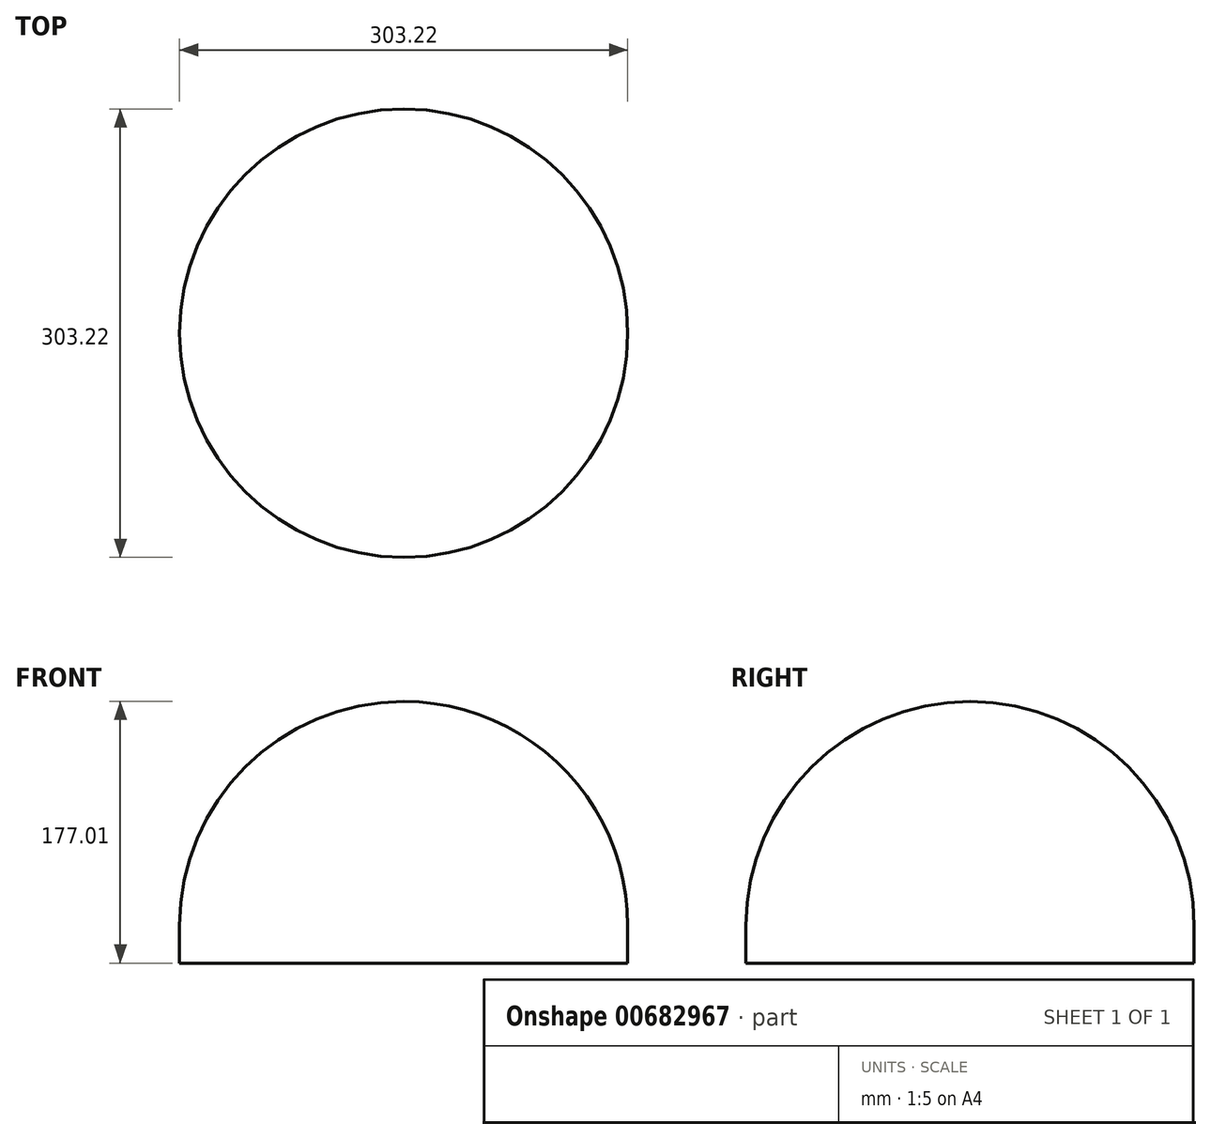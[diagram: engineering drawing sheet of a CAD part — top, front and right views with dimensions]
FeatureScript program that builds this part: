
annotation { "Feature Type Name" : "Feature", "Feature Type Description" : "" }
export const myFeature = defineFeature(function(context is Context, id is Id, definition is map)
    precondition{}
    {
        {
            var Q0;
            Q0=qCreatedBy(makeId("Front.planeOp"),FACE);
            var sketch = newSketch(context, id + "F0", { "sketchPlane" : qUnion([Q0])});
            skArc(sketch, "E0", {"start": v(151.6, 0) * mm, "mid": v(107.2, 107.2) * mm, "end": v(0, 151.6) * mm});
            skCircle(sketch, "E1", {"center": v(580.93, 2.93) * mm, "radius": 152.4 * mm});
            skLineSegment(sketch, "E2", {"start": v(0, 0) * mm, "end": v(0, 151.6) * mm});
            skLineSegment(sketch, "E3", {"start": v(151.6, 0) * mm, "end": v(151.6, -25.4) * mm});
            skLineSegment(sketch, "E4", {"start": v(151.6, -25.4) * mm, "end": v(0, -25.4) * mm});
            skLineSegment(sketch, "E5", {"start": v(0, -25.4) * mm, "end": v(0, 0) * mm});
            skLineSegment(sketch, "E6", {"start": v(733.3, 0) * mm, "end": v(733.3, 25.4) * mm});
            skLineSegment(sketch, "E7", {"start": v(733.3, 25.4) * mm, "end": v(885.7, 25.4) * mm});
            skLineSegment(sketch, "E8", {"start": v(885.7, 25.4) * mm, "end": v(885.7, -228.6) * mm});
            skLineSegment(sketch, "E9", {"start": v(885.7, -228.6) * mm, "end": v(580.93, -228.6) * mm});
            skLineSegment(sketch, "E10.MirrorCS", {"start": v(276.15, 25.4) * mm, "end": v(276.15, -228.6) * mm});
            skLineSegment(sketch, "E11.MirrorCS", {"start": v(276.15, -228.6) * mm, "end": v(580.93, -228.6) * mm});
            skLineSegment(sketch, "E12.MirrorCS", {"start": v(428.55, 25.4) * mm, "end": v(276.15, 25.4) * mm});
            skLineSegment(sketch, "E13.MirrorCS", {"start": v(428.55, 0) * mm, "end": v(428.55, 25.4) * mm});
            skLineSegment(sketch, "E14.MirrorCS", {"start": v(580.93, -228.6) * mm, "end": v(580.93, 26.87) * mm});
            skLineSegment(sketch, "E15", {"start": v(733.3, 25.4) * mm, "end": v(428.55, 25.4) * mm});
            skSolve(sketch);
        }
        {
            var Q0;
            Q0=makeQuery(id+"F0.imprint","IMPRINT",FACE,{"disambiguationData":[TD([[makeQuery(id+"F0.imprint","IMPRINT",EDGE,{"derivedFrom":sQuery(id+"F0.wireOp",EDGE,"E0")}),1.0]])]});
            var Q1;
            Q1=sQuery(id+"F0.wireOp",EDGE,"E2");
            revolve(context, id + "F1", {"surfaceOperationType" : NewSurfaceOperationType.NEW, "entities" : qUnion([Q0]), "axis" : qUnion([Q1]), "revolveType" : RevolveType.FULL});
        }
    });
